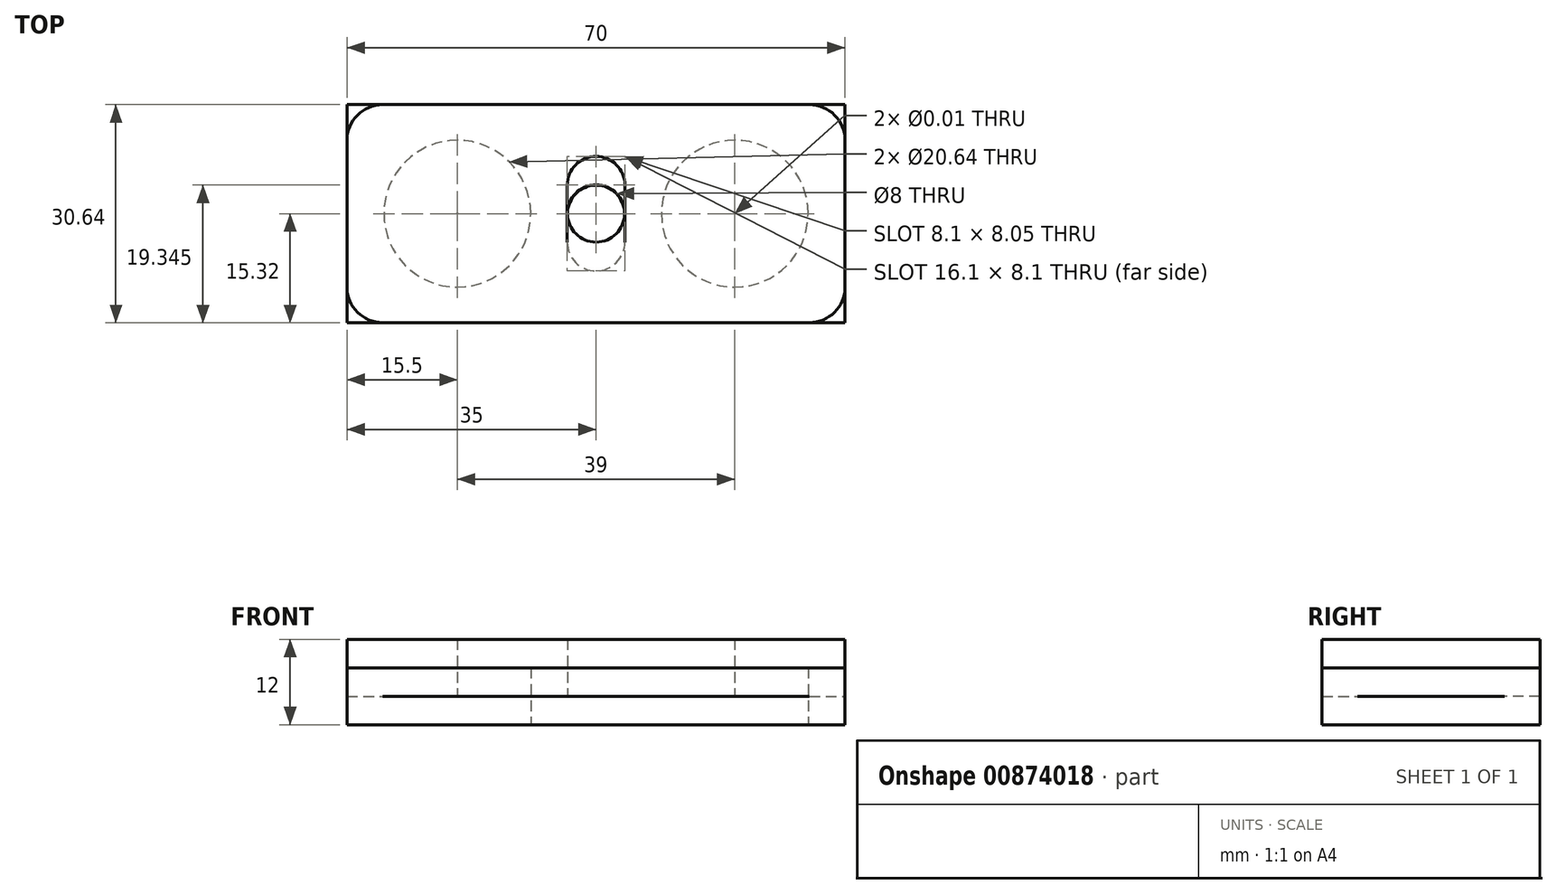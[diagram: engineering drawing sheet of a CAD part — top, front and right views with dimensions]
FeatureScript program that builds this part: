
annotation { "Feature Type Name" : "Feature", "Feature Type Description" : "" }
export const myFeature = defineFeature(function(context is Context, id is Id, definition is map)
    precondition{}
    {
        {
            var Q0;
            Q0=qCreatedBy(makeId("Top.planeOp"),FACE);
            var sketch = newSketch(context, id + "F0", { "sketchPlane" : qUnion([Q0])});
            skLineSegment(sketch, "E0.bottom", {"start": v(35, -15.32) * mm, "end": v(-35, -15.32) * mm});
            skLineSegment(sketch, "E0.top", {"start": v(35, 15.32) * mm, "end": v(-35, 15.32) * mm});
            skLineSegment(sketch, "E0.left", {"start": v(35, -15.32) * mm, "end": v(35, 15.32) * mm});
            skLineSegment(sketch, "E0.right", {"start": v(-35, -15.32) * mm, "end": v(-35, 15.32) * mm});
            skPoint(sketch, "E0.middle", {"position": v(0, 0) * mm});
            skLineSegment(sketch, "E1", {"start": v(0, 0) * mm, "end": v(0, 4) * mm});
            skLineSegment(sketch, "E2", {"start": v(0, 0) * mm, "end": v(0, -4) * mm});
            skArc(sketch, "E3.0.startCap", {"start": v(4.05, 0) * mm, "mid": v(0, -4.05) * mm, "end": v(-4.05, 0) * mm});
            skArc(sketch, "E3.0.endCap", {"start": v(-4.05, 4) * mm, "mid": v(0, 8.05) * mm, "end": v(4.05, 4) * mm});
            skLineSegment(sketch, "E3.0.left", {"start": v(-4.05, 0) * mm, "end": v(-4.05, 4) * mm});
            skLineSegment(sketch, "E3.0.right", {"start": v(4.05, 0) * mm, "end": v(4.05, 4) * mm});
            skArc(sketch, "E3.1.startCap", {"start": v(-4.05, 0) * mm, "mid": v(0, 4.05) * mm, "end": v(4.05, 0) * mm});
            skArc(sketch, "E3.1.endCap", {"start": v(4.05, -4) * mm, "mid": v(0, -8.05) * mm, "end": v(-4.05, -4) * mm});
            skLineSegment(sketch, "E3.1.left", {"start": v(4.05, 0) * mm, "end": v(4.05, -4) * mm});
            skLineSegment(sketch, "E3.1.right", {"start": v(-4.05, 0) * mm, "end": v(-4.05, -4) * mm});
            skCircle(sketch, "E4", {"center": v(19.5, 0) * mm, "radius": 10.32 * mm});
            skCircle(sketch, "E5", {"center": v(-19.5, 0) * mm, "radius": 10.32 * mm});
            skSolve(sketch);
        }
        {
            var Q0;
            Q0=makeQuery(id+"F0.imprint","IMPRINT",FACE,{"disambiguationData":[TD([[makeQuery(id+"F0.imprint","IMPRINT",EDGE,{"derivedFrom":sQuery(id+"F0.wireOp",EDGE,"E0.bottom")}),-1.0]])]});
            extrude(context, id + "F1", {"entities" : qUnion([Q0]), "endBound" : BoundingType.SYMMETRIC, "depth" : 8 * mm, "offsetDistance" : 25 * mm});
        }
        {
            var Q0;
            Q0 = qSketchRegion(id + "F0", true);
            var Q1;
            Q1=makeQuery(id+"F0.imprint","IMPRINT",FACE,{"disambiguationData":[TD([[makeQuery(id+"F0.imprint","IMPRINT",EDGE,{"derivedFrom":sQuery(id+"F0.wireOp",EDGE,"E5")}),1.0]])]});
            var Q2;
            Q2=makeQuery(id+"F0.imprint","IMPRINT",FACE,{"disambiguationData":[TD([[makeQuery(id+"F0.imprint","IMPRINT",EDGE,{"derivedFrom":sQuery(id+"F0.wireOp",EDGE,"E3.0.startCap")}),1.0]])]});
            var Q3;
            Q3=makeQuery(id+"F0.imprint","IMPRINT",FACE,{"disambiguationData":[TD([[makeQuery(id+"F0.imprint","IMPRINT",EDGE,{"derivedFrom":sQuery(id+"F0.wireOp",EDGE,"E3.0.startCap")}),-1.0]])]});
            var Q4;
            Q4=makeQuery(id+"F0.imprint","IMPRINT",FACE,{"disambiguationData":[TD([[makeQuery(id+"F0.imprint","IMPRINT",EDGE,{"derivedFrom":sQuery(id+"F0.wireOp",EDGE,"E3.0.endCap")}),-1.0]])]});
            var Q5;
            Q5=makeQuery(id+"F0.imprint","IMPRINT",FACE,{"disambiguationData":[TD([[makeQuery(id+"F0.imprint","IMPRINT",EDGE,{"derivedFrom":sQuery(id+"F0.wireOp",EDGE,"E4")}),1.0]])]});
            extrude(context, id + "F2", {"entities" : qUnion([Q0, Q1, Q2, Q3, Q4, Q5]), "depth" : 8 * mm, "offsetDistance" : 25 * mm});
        }
        {
            var Q0;
            Q0=sQuery(id+"F0.wireOp",VERTEX,"E5.center");
            var Q1;
            Q1=sQuery(id+"F0.wireOp",VERTEX,"E4.center");
            var Q2;
            Q2=makeQuery(id+"F2.opExtrude","SWEPT_BODY",BODY,{"disambiguationData":[OSD([sQuery(id+"F0.wireOp",EDGE,"E0.bottom"),sQuery(id+"F0.wireOp",EDGE,"E0.top"),sQuery(id+"F0.wireOp",EDGE,"E0.left"),sQuery(id+"F0.wireOp",EDGE,"E0.right")])]});
            hole(context, id + "F3", {"style" : HoleStyle.SIMPLE, "endStyle" : HoleEndStyle.THROUGH, "oppositeDirection" : true, "standardTappedOrClearance" : lookupTablePath({ "standard" : "ANSI", "size" : "3/8 (0.38)", "type" : "Drilled" }), "standardBlindInLast" : lookupTablePath({ "standard" : "ANSI", "size" : "3/8", "type" : "Drilled" }), "holeDiameter" : 3 / 203.2 * mm, "majorDiameter" : 5 * mm, "isTappedThrough" : true, "tappedDepth" : 12 * mm, "tapClearance" : 3, "locations" : qUnion([Q0, Q1]), "scope" : qUnion([Q2])});
        }
        {
            var Q0;
            Q0=sQuery(id+"F0.wireOp",VERTEX,"E0.middle");
            var Q1;
            Q1=makeQuery(id+"F2.opExtrude","SWEPT_BODY",BODY,{"disambiguationData":[OSD([sQuery(id+"F0.wireOp",EDGE,"E0.bottom"),sQuery(id+"F0.wireOp",EDGE,"E0.top"),sQuery(id+"F0.wireOp",EDGE,"E0.left"),sQuery(id+"F0.wireOp",EDGE,"E0.right")])]});
            hole(context, id + "F4", {"style" : HoleStyle.SIMPLE, "endStyle" : HoleEndStyle.THROUGH, "oppositeDirection" : true, "standardTappedOrClearance" : lookupTablePath({ "standard" : "ISO", "size" : "8", "type" : "Drilled" }), "standardBlindInLast" : lookupTablePath({ "standard" : "ISO", "size" : "8", "type" : "Drilled" }), "holeDiameter" : 8 * mm, "majorDiameter" : 5 * mm, "isTappedThrough" : true, "tappedDepth" : 12 * mm, "tapClearance" : 3, "locations" : qUnion([Q0]), "scope" : qUnion([Q1])});
        }
        {
            var Q0;
            Q0=makeQuery(id+"F2.opExtrude","SWEPT_EDGE",EDGE,{"disambiguationData":[OSD([sQuery(id+"F0.wireOp",EDGE,"E0.top"),sQuery(id+"F0.wireOp",EDGE,"E0.right")])]});
            var Q1;
            Q1=makeQuery(id+"F2.opExtrude","SWEPT_EDGE",EDGE,{"disambiguationData":[OSD([sQuery(id+"F0.wireOp",EDGE,"E0.top"),sQuery(id+"F0.wireOp",EDGE,"E0.left")])]});
            var Q2;
            Q2=makeQuery(id+"F2.opExtrude","SWEPT_EDGE",EDGE,{"disambiguationData":[OSD([sQuery(id+"F0.wireOp",EDGE,"E0.bottom"),sQuery(id+"F0.wireOp",EDGE,"E0.right")])]});
            var Q3;
            Q3=makeQuery(id+"F2.opExtrude","SWEPT_EDGE",EDGE,{"disambiguationData":[OSD([sQuery(id+"F0.wireOp",EDGE,"E0.bottom"),sQuery(id+"F0.wireOp",EDGE,"E0.left")])]});
            fillet(context, id + "F5", {"entities" : qUnion([Q0, Q1, Q2, Q3]), "radius" : (13 / 406.4 * mm + 2 * 5 * mm) / 2, "tangentPropagation" : true, "allowEdgeOverflow" : false});
        }
    });
